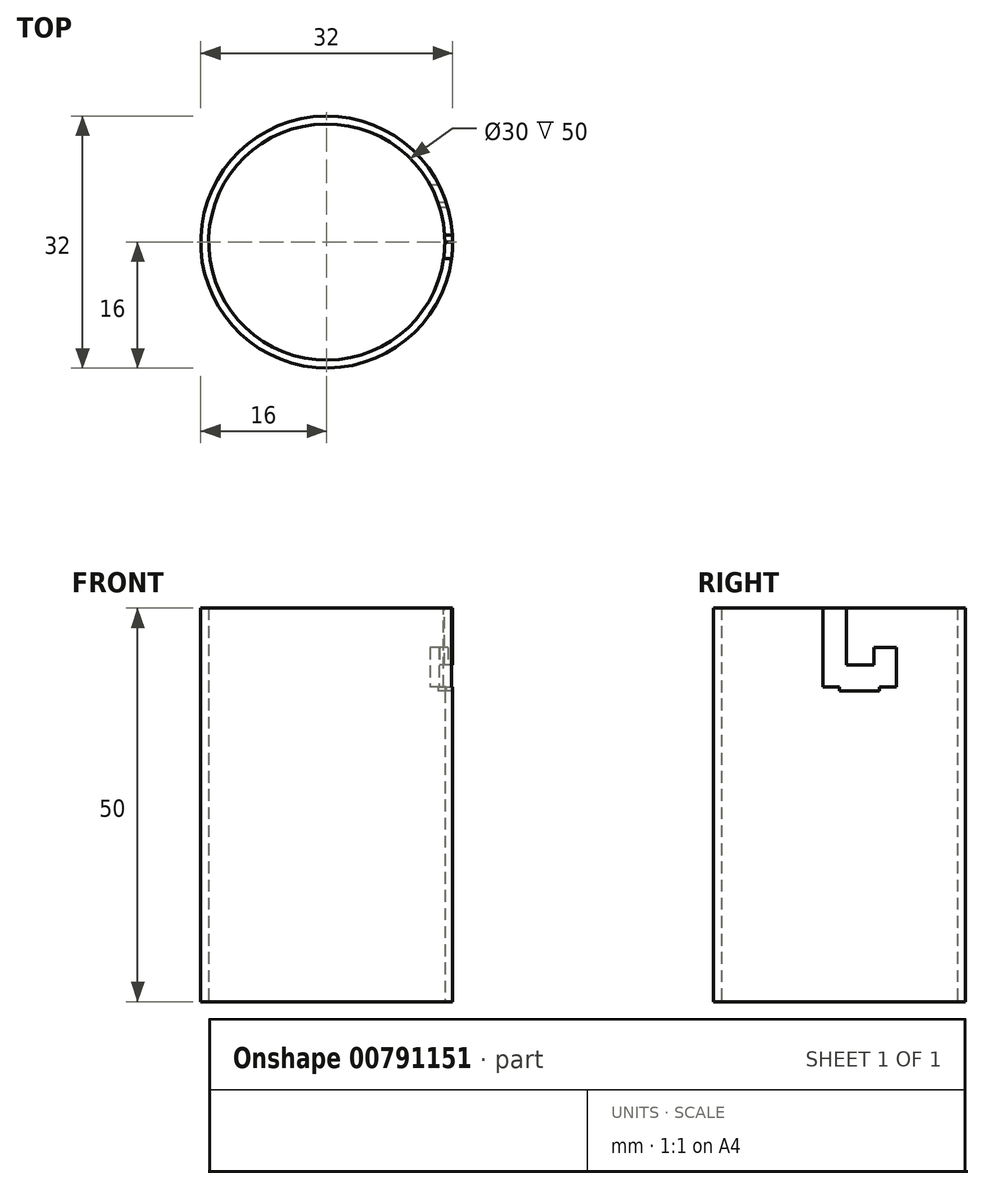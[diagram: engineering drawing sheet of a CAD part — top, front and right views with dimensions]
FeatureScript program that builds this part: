
annotation { "Feature Type Name" : "Feature", "Feature Type Description" : "" }
export const myFeature = defineFeature(function(context is Context, id is Id, definition is map)
    precondition{}
    {
        {
            var Q0;
            Q0=qCreatedBy(makeId("Top.planeOp"),FACE);
            var sketch = newSketch(context, id + "F0", { "sketchPlane" : qUnion([Q0])});
            skCircle(sketch, "E0", {"center": v(0, 0) * mm, "radius": 15 * mm});
            skCircle(sketch, "E1.0", {"center": v(0, 0) * mm, "radius": 16 * mm});
            skSolve(sketch);
        }
        {
            var Q0;
            Q0=makeQuery(id+"F0.imprint","IMPRINT",FACE,{"disambiguationData":[TD([[makeQuery(id+"F0.imprint","IMPRINT",EDGE,{"derivedFrom":sQuery(id+"F0.wireOp",EDGE,"E0")}),-1.0]])]});
            extrude(context, id + "F1", {"entities" : qUnion([Q0]), "depth" : 50 * mm, "offsetDistance" : 25 * mm});
        }
        {
            var Q0;
            Q0=makeQuery(id+"F1.opExtrude","CAP_FACE",FACE,{"disambiguationData":[OSD([sQuery(id+"F0.wireOp",EDGE,"E0"),sQuery(id+"F0.wireOp",EDGE,"E1.0")])],"isStart":false});
            var sketch = newSketch(context, id + "F2", { "sketchPlane" : qUnion([Q0])});
            skLineSegment(sketch, "E2.bottom", {"start": v(13.82, 0.9) * mm, "end": v(16.93, 0.9) * mm});
            skLineSegment(sketch, "E2.top", {"start": v(13.82, -2.1) * mm, "end": v(16.93, -2.1) * mm});
            skLineSegment(sketch, "E2.left", {"start": v(13.82, 0.9) * mm, "end": v(13.82, -2.1) * mm});
            skLineSegment(sketch, "E2.right", {"start": v(16.93, 0.9) * mm, "end": v(16.93, -2.1) * mm});
            skSolve(sketch);
        }
        {
            var Q0;
            {var subQ0=sQuery(id+"F2.wireOp",EDGE,"E2.bottom");var subQ1=makeQuery(id+"F1.opExtrude","CAP_EDGE",EDGE,{"disambiguationData":[OSD([sQuery(id+"F0.wireOp",EDGE,"E1.0")])],"isStart":false});var subQ2=makeQuery(id+"F2.imprint","INTERSECT",VERTEX,{"derivedFrom":[subQ1,subQ0]});Q0=makeQuery(id+"F2.imprint","IMPRINT",FACE,{"disambiguationData":[TD([[makeQuery(id+"F2.imprint","IMPRINT",EDGE,{"disambiguationData":[TD([[subQ2,1.0]])],"derivedFrom":subQ0}),-1.0]])]});}
            extrude(context, id + "F3", {"entities" : qUnion([Q0]), "operationType" : NewBodyOperationType.REMOVE, "oppositeDirection" : true, "depth" : 10 * mm, "offsetDistance" : 25 * mm});
        }
        {
            var Q0;
            Q0=qCreatedBy(makeId("Top.planeOp"),FACE);
            cPlane(context, id + "F4", {"entities" : qUnion([Q0]), "cplaneType" : CPlaneType.OFFSET, "offset" : 40 * mm, "width" : 150 * mm, "height" : 150 * mm});
        }
        {
            var Q0;
            Q0=qCreatedBy(id+"F4.planeOp",FACE);
            var sketch = newSketch(context, id + "F5", { "sketchPlane" : qUnion([Q0])});
            skLineSegment(sketch, "E3.bottom", {"start": v(16.69, 7.25) * mm, "end": v(12.13, 7.25) * mm});
            skLineSegment(sketch, "E3.top", {"start": v(16.69, 4.35) * mm, "end": v(12.13, 4.35) * mm});
            skLineSegment(sketch, "E3.left", {"start": v(16.69, 7.25) * mm, "end": v(16.69, 4.35) * mm});
            skLineSegment(sketch, "E3.right", {"start": v(12.13, 7.25) * mm, "end": v(12.13, 4.35) * mm});
            skSolve(sketch);
        }
        {
            var Q0;
            Q0 = qSketchRegion(id + "F5", true);
            extrude(context, id + "F6", {"entities" : qUnion([Q0]), "operationType" : NewBodyOperationType.REMOVE, "depth" : 5 * mm, "offsetDistance" : 25 * mm});
        }
        {
            var Q0;
            Q0=qCreatedBy(makeId("Right.planeOp"),FACE);
            var sketch = newSketch(context, id + "F7", { "sketchPlane" : qUnion([Q0])});
            skLineSegment(sketch, "E4.bottom", {"start": v(0, 39.47) * mm, "end": v(5.09, 39.47) * mm});
            skLineSegment(sketch, "E4.top", {"start": v(0, 42.78) * mm, "end": v(5.09, 42.78) * mm});
            skLineSegment(sketch, "E4.left", {"start": v(0, 39.47) * mm, "end": v(0, 42.78) * mm});
            skLineSegment(sketch, "E4.right", {"start": v(5.09, 39.47) * mm, "end": v(5.09, 42.78) * mm});
            skSolve(sketch);
        }
        {
            var Q0;
            Q0=makeQuery(id+"F7.imprint","IMPRINT",FACE,{"disambiguationData":[TD([[makeQuery(id+"F7.imprint","IMPRINT",EDGE,{"derivedFrom":sQuery(id+"F7.wireOp",EDGE,"E4.bottom")}),1.0]])]});
            extrude(context, id + "F8", {"entities" : qUnion([Q0]), "operationType" : NewBodyOperationType.REMOVE, "depth" : 49.4 * mm, "offsetDistance" : 25 * mm});
        }
    });
